# Revit family: BrushHolder-Vitra-OriginSeries-A44894
name_source: partatom
category: Plumbing Fixtures
revit_build: Autodesk Revit 2017 (Build: 20160225_1515(x64)
units: mm (PartAtom-declared; Revit-internal decimal feet)

## family parameters
Cut with Voids When Loaded = No
Host = Face
OmniClass Number = 23.45.55.17
OmniClass Title = Mixing Faucets
Part Type = Normal
Room Calculation Point = No
Round Connector Dimension = Use Diameter
Shared = Yes

## types (4) — shared parameters
BIMobject category = Accessories
CW Connection = No
Depth(mm) = 77 mm  [stored 0.252625 ft]
Description = Origin Wc Brush Holder Wall
Design country = Turkey
HW Connection = No
Height(mm) = 397 mm  [stored 1.30249 ft]
IFC Classification = Sanitary Terminal
Manufacturer = Vitra
Manufacturer name = Vitra
Masterformat 2014 Code = 10 28 13
Masterformat 2014 Description = Toilet Accessories
MountingType = Wall Mounted
NBS Referans Code = 35-75-86
NBS Referans Description = Toilet Brush Holders
Nominal height = 0.000
Nominal width = 0.000
OmniClass Code = 23-31 25 00
OmniClass Description = Toilet and Bath Specialties
Product Type = Wc Brush Holder Wall
Product certification = https://vitraglobal.com
Product data url = https://www.vitraglobal.com
Product family = Origin
Product group = Origin WC Brush Holder
Technical description = https://www.vitra.com.tr
UNSPSC Code = 3018
UNSPSC Description = Plumbing Fixtures
URL = https://vitraglobal.com
Uniclass 1.4 Code = L7313
Uniclass 1.4 Description = Sanitary above ground pipes and fittings
Uniclass 2.0 Code = PR-35-75-86
Uniclass 2.0 Description = Toilet Brush Holders
Uniclass 2015 Code = PR_40_20_76_86
Uniclass 2015 Name = Toilet Brush Holders
Uniformat II Code = D2010
Uniformat II Description = Plumbing Fixtures
Warranty Period (Year) = 5 Years
Waste Connection = No
Weight Net (kg) = 1,150
Width(mm) = 70 mm  [stored 0.229659 ft]
Youtube = https://www.youtube.com
zero-valued in all types: Cost, Default Elevation

## per-type parameters (varying)
| type | Article No. (default) | Coating Material | Color | Model | Product SKU |
| WCBrushHolder-Vitra-OriginSeries(Chrome)-A44894 | A44894 | Vitra-Chrome | Chrome | A44894 | A44894 |
| WCBrushHolder-Vitra-OriginSeries(Copper)-A4489426 | A4489426 | Vitra-Copper | Copper | A4489426 | A4489426 |
| WCBrushHolder-Vitra-OriginSeries(BrushedNickel)-A4489434 | A4489434 | Vitra-Brushed Nickel | Brushed Nickel | A4489434 | A4489434 |
| WCBrushHolder-Vitra-OriginSeries(Black)-A4489436 | A4489436 | Vitra-Black | Black | A4489436 | A4489436 |

note: [stored X ft] marks values corroborated as IEEE doubles in the binary element streams (Revit-internal decimal feet)

## geometry (parser evidence)
native form markers: Sweep x3
no freeform markers — native parametric forms only
